# Revit family: QF_MACOM_HOSIM30CA-2M
name_source: partatom
category: Equipamento especial
units: mm (PartAtom-declared; Revit-internal decimal feet)

## family parameters
Com base no plano de trabalho = Não
Compartilhado = Não
Corte com vazios quando carregada = Não
Cota do conector redondo = Utilizar diâmetro
Número OmniClass = 23.40.40.14.27
Ponto de cálculo do ambiente = Não
Sempre na vertical = Sim
Tipo de parte = Normal
Título OmniClass = Ice Machines

## types (1)
- HOSIM30CA-2M
    Apparent Power = 0 VA
    Cold Water Connection Height = 0 mm
    Cold Water Flow = 0,0 L/s
    Cold Water Maximum Pressure = 0,0 Pa
    Cold Water Minimum Pressure = 0,0 Pa
    Cold Water RI Height = 0 mm
    Cold Water Size = 1/2"
    Cold Water Temperature Recommended = -273 °C
    Conn Conduit = Sim
    Descrição = MAQUINA DE GELO EM CUBO HOSHIZAKI, PRODUCAO ATE 28KG/DIA, COM DEPOSITO DE 12KG - 220V MONOF - IM30CA-398X510X785mm
    Elec Conn RI Height = 0 mm
    Elevação padrão = 0 mm
    FL Amps = 0 A
    Fabricante = MACOM
    Indirect Waste Connection Height = 151 mm
    Indirect Waste Flow = 0,0 L/s
    Indirect Waste Size = 22,00 mm
    Max Overcurrent Protection = 0 A
    Min Ckt Ampacity = 0 A
    Modelo = HOSIM30CA-2M
    Number of Poles = 0
    Production per Cycle = 18 cubes
    Production per day = 22kg to 27kg
    Room Temperature = 10°C to 32°C
    Storage = 12,00 kg
    URL = https://www.acosmacom.com.br
    Volume = 0,16 m³
    Waste Water Discharge Temperature = -273 °C
    Water Consumption = 60L to 160L
    Water Temperature = 10°C to 21°C

## geometry (parser evidence)
native form markers: Blend x4, Sweep x2
no freeform markers — native parametric forms only
